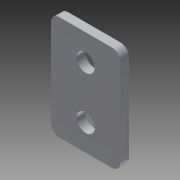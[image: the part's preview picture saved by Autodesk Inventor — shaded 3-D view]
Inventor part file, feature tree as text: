
AUTODESK INVENTOR PART (.ipt)
format: ipt  version: 2013 (Build 170138000, 138)  size: 93,184 bytes
history: native  units: in
note: dims shown in document units (in); Inventor stores cm internally (conversion verified against a paired STEP export)
features: extrude x1, fillet x1, sketch x1
ambient origin geometry x8: Origin, YZ Plane, XZ Plane, XY Plane, X Axis, Y Axis, Z Axis, Center Point
bodies: Solid1 (feature_tree)
feature tree (3):
  extrude  "Extrusion1"  Depth=1.5in
  fillet  "Fillet1"  Radius=0.26in
  sketch  "Sketch1"  dims[d0=1.0in d2=1.5in d3=0.26in d4=0.75in d5=0.375in d6=0.125in d7=0.0in d8=0.125in d9=0.375in]
